# Revit family: Тактильная полиуретановая плитка прямы полосы (приклеивание)
name_source: partatom
category: Оборудование
revit_build: Autodesk Revit 2017 (Build: 20160225_1515(x64)
units: mm (PartAtom-declared; Revit-internal decimal feet)

## family parameters
Общий = Да
Основа = Грань
При загрузке вырезать с полостями = Да
Размер круглого соединителя = Использовать диаметр
Тип детали = Нормальный
Точка расчета площади = Нет

## types (2) — shared parameters
ADSK_Наименование = Тактильная полиуретановая плитка с прямыми рельефными полосами (приклеивание)
ADSK_Размер_Высота рифа = 5 мм
ADSK_Размер_Габариты = 300Х300
ADSK_Размер_Длина = 300 мм
ADSK_Размер_Толщина = 2 мм
ADSK_Размер_Ширина = 300 мм
ADSK_Тип рифов = Рельефные полосы
URL = http://tiflocentre.ru
Изготовитель = ТИФЛОЦЕНТР «ВЕРТИКАЛЬ»
Применение = Улица/Помещение
Стоимость = 378 $
zero-valued in all types: Отметка по умолчанию

## per-type parameters (varying)
| type | ADSK_Код изделия | ADSK_Материал наименование | ADSK_Материал плитки | Описание |
| Тактильная плитка полиуретан_Желтая | 10130-ZH | Полиуретан, цвет желтый | Вертикаль_Полиуретан_Желтый | Тактильная ПУ плитка предназначена для обеспечения информирования при движении людей с ограничениями зрения как в помещениях, так и на улице. Расположение тактильных рифов в виде параллельных полос "говорит" незрячему человеку о движении прямо без препятствий на пути. Желтый цвет плитки отлично контрастирует с темной поверхностью асфальта и кафеля, что рекомендовано программой "Доступная среда". Тактильная ПУ плитка не требует трудоемкого монтажа, ее достаточно просто посадить на клей, заранее очистив поверхность. |
| Тактильная плитка полиуретановая_Черная | 10130-CH | Полиуретан, цвет черный | Вертикаль_Полиуретан_Черный | Тактильная ПУ плитка информирует человека с ограничениями зрения во время движения. Благодаря своим прочностным характеристикам и устойчивости, тактильную ПУ плитку можно монтировать как в помещениях, так и на улице.  Рельефные полосы на тактильной плитке информируют незрячего человека о движении прямо без ограничений. Тактильная плитка черного цвета применяется для организации контраста на светлых поверхностях, что особенно важно для слабовидящего человека. |
